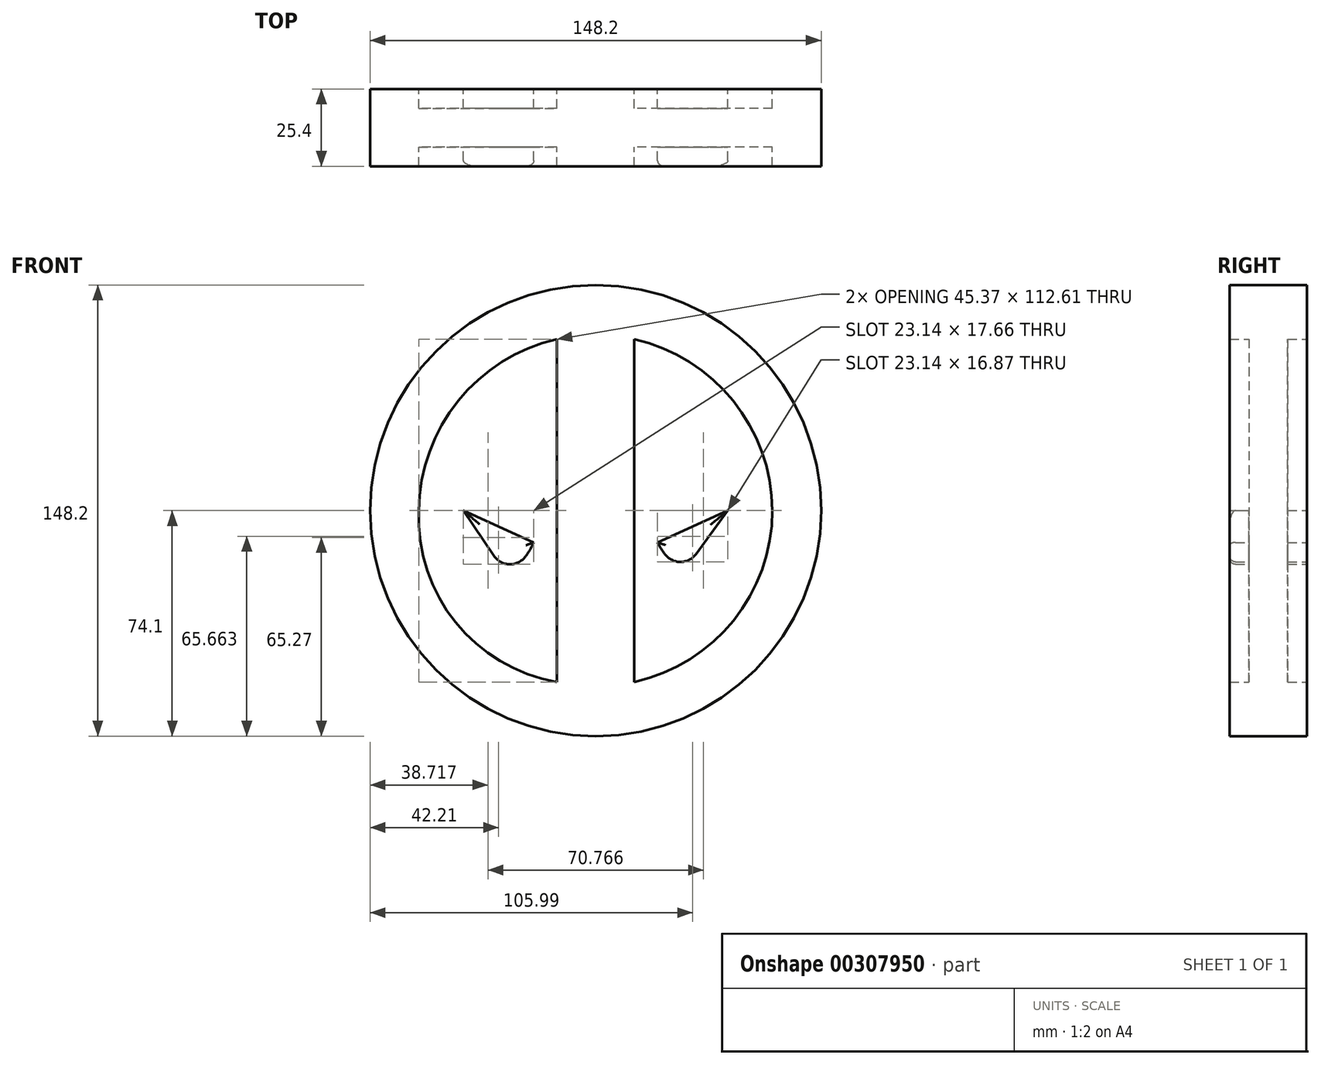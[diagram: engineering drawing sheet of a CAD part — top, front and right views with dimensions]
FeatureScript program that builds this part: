
annotation { "Feature Type Name" : "Feature", "Feature Type Description" : "" }
export const myFeature = defineFeature(function(context is Context, id is Id, definition is map)
    precondition{}
    {
        {
            var Q0;
            Q0=qCreatedBy(makeId("Front.planeOp"),FACE);
            var sketch = newSketch(context, id + "F0", { "sketchPlane" : qUnion([Q0])});
            skCircle(sketch, "E0", {"center": v(0, 0) * mm, "radius": 74.1 * mm});
            skLineSegment(sketch, "E1", {"start": v(-12.7, 56.3) * mm, "end": v(-12.7, -56.3) * mm});
            skArc(sketch, "E2", {"start": v(-12.7, 56.3) * mm, "mid": v(-45.17, 36.04) * mm, "end": v(-58.07, 0) * mm});
            skArc(sketch, "E3", {"start": v(-58.07, 0) * mm, "mid": v(-46, -36.7) * mm, "end": v(-12.7, -56.3) * mm});
            skLineSegment(sketch, "E4", {"start": v(12.7, 56.3) * mm, "end": v(12.7, -56.3) * mm});
            skArc(sketch, "E5", {"start": v(12.7, -56.3) * mm, "mid": v(45.26, -36.1) * mm, "end": v(58.07, 0) * mm});
            skArc(sketch, "E6", {"start": v(58.07, 0) * mm, "mid": v(45.17, 36.04) * mm, "end": v(12.7, 56.3) * mm});
            skLineSegment(sketch, "E7", {"start": v(20.32, -10.47) * mm, "end": v(43.46, 0) * mm});
            skLineSegment(sketch, "E8", {"start": v(-20.32, -10.47) * mm, "end": v(-43.46, 0) * mm});
            skArc(sketch, "E9", {"start": v(-20.32, -10.47) * mm, "mid": v(-21.55, -12.85) * mm, "end": v(-23.02, -15.08) * mm});
            skLineSegment(sketch, "E10", {"start": v(-33.4, -14.87) * mm, "end": v(-43.46, 0) * mm});
            skArc(sketch, "E11", {"start": v(20.32, -10.47) * mm, "mid": v(21.51, -12.58) * mm, "end": v(22.93, -14.53) * mm});
            skLineSegment(sketch, "E12", {"start": v(32.98, -14.28) * mm, "end": v(43.46, 0) * mm});
            skPoint(sketch, "E13.visualSharp", {"position": v(-29.22, -21.03) * mm});
            skArc(sketch, "E13.filletArc", {"start": v(-33.4, -14.87) * mm, "mid": v(-28.26, -17.66) * mm, "end": v(-23.02, -15.08) * mm});
            skPoint(sketch, "E14.visualSharp", {"position": v(29, -19.7) * mm});
            skArc(sketch, "E14.filletArc", {"start": v(22.93, -14.53) * mm, "mid": v(28.01, -16.87) * mm, "end": v(32.98, -14.28) * mm});
            skSolve(sketch);
        }
        {
            var Q0;
            Q0=makeQuery(id+"F0.imprint","IMPRINT",FACE,{"disambiguationData":[TD([[makeQuery(id+"F0.imprint","IMPRINT",EDGE,{"derivedFrom":sQuery(id+"F0.wireOp",EDGE,"E0")}),1.0]])]});
            extrude(context, id + "F1", {"entities" : qUnion([Q0]), "endBound" : BoundingType.SYMMETRIC, "depth" : 25.4 * mm});
        }
        {
            var Q0;
            Q0=makeQuery(id+"F0.imprint","IMPRINT",FACE,{"disambiguationData":[TD([[makeQuery(id+"F0.imprint","IMPRINT",EDGE,{"derivedFrom":sQuery(id+"F0.wireOp",EDGE,"E1")}),-1.0]])]});
            var Q1;
            Q1=makeQuery(id+"F0.imprint","IMPRINT",FACE,{"disambiguationData":[TD([[makeQuery(id+"F0.imprint","IMPRINT",EDGE,{"derivedFrom":sQuery(id+"F0.wireOp",EDGE,"E4")}),1.0]])]});
            extrude(context, id + "F2", {"entities" : qUnion([Q0, Q1]), "operationType" : NewBodyOperationType.ADD, "endBound" : BoundingType.SYMMETRIC, "depth" : 12.7 * mm});
        }
        {
            var Q0;
            Q0=makeQuery(id+"F0.imprint","IMPRINT",FACE,{"disambiguationData":[TD([[makeQuery(id+"F0.imprint","IMPRINT",EDGE,{"derivedFrom":sQuery(id+"F0.wireOp",EDGE,"E8")}),1.0]])]});
            var Q1;
            Q1=makeQuery(id+"F0.imprint","IMPRINT",FACE,{"disambiguationData":[TD([[makeQuery(id+"F0.imprint","IMPRINT",EDGE,{"derivedFrom":sQuery(id+"F0.wireOp",EDGE,"E7")}),-1.0]])]});
            extrude(context, id + "F3", {"entities" : qUnion([Q0, Q1]), "operationType" : NewBodyOperationType.ADD, "endBound" : BoundingType.SYMMETRIC, "depth" : 25.4 * mm});
        }
        {
            var Q0;
            Q0=makeQuery(id+"F3.opExtrude","CAP_EDGE",EDGE,{"disambiguationData":[OSD([sQuery(id+"F0.wireOp",EDGE,"E10")])],"isStart":false});
            var Q1;
            Q1=makeQuery(id+"F3.opExtrude","CAP_EDGE",EDGE,{"disambiguationData":[OSD([sQuery(id+"F0.wireOp",EDGE,"E12")])],"isStart":false});
            var Q2;
            Q2=makeQuery(id+"F3.opExtrude","CAP_EDGE",EDGE,{"disambiguationData":[OSD([sQuery(id+"F0.wireOp",EDGE,"E8")])],"isStart":false});
            var Q3;
            Q3=makeQuery(id+"F3.opExtrude","CAP_EDGE",EDGE,{"disambiguationData":[OSD([sQuery(id+"F0.wireOp",EDGE,"E7")])],"isStart":false});
            fillet(context, id + "F4", {"entities" : qUnion([Q0, Q1, Q2, Q3]), "radius" : 1.9 * mm, "tangentPropagation" : true, "allowEdgeOverflow" : false});
        }
    });
